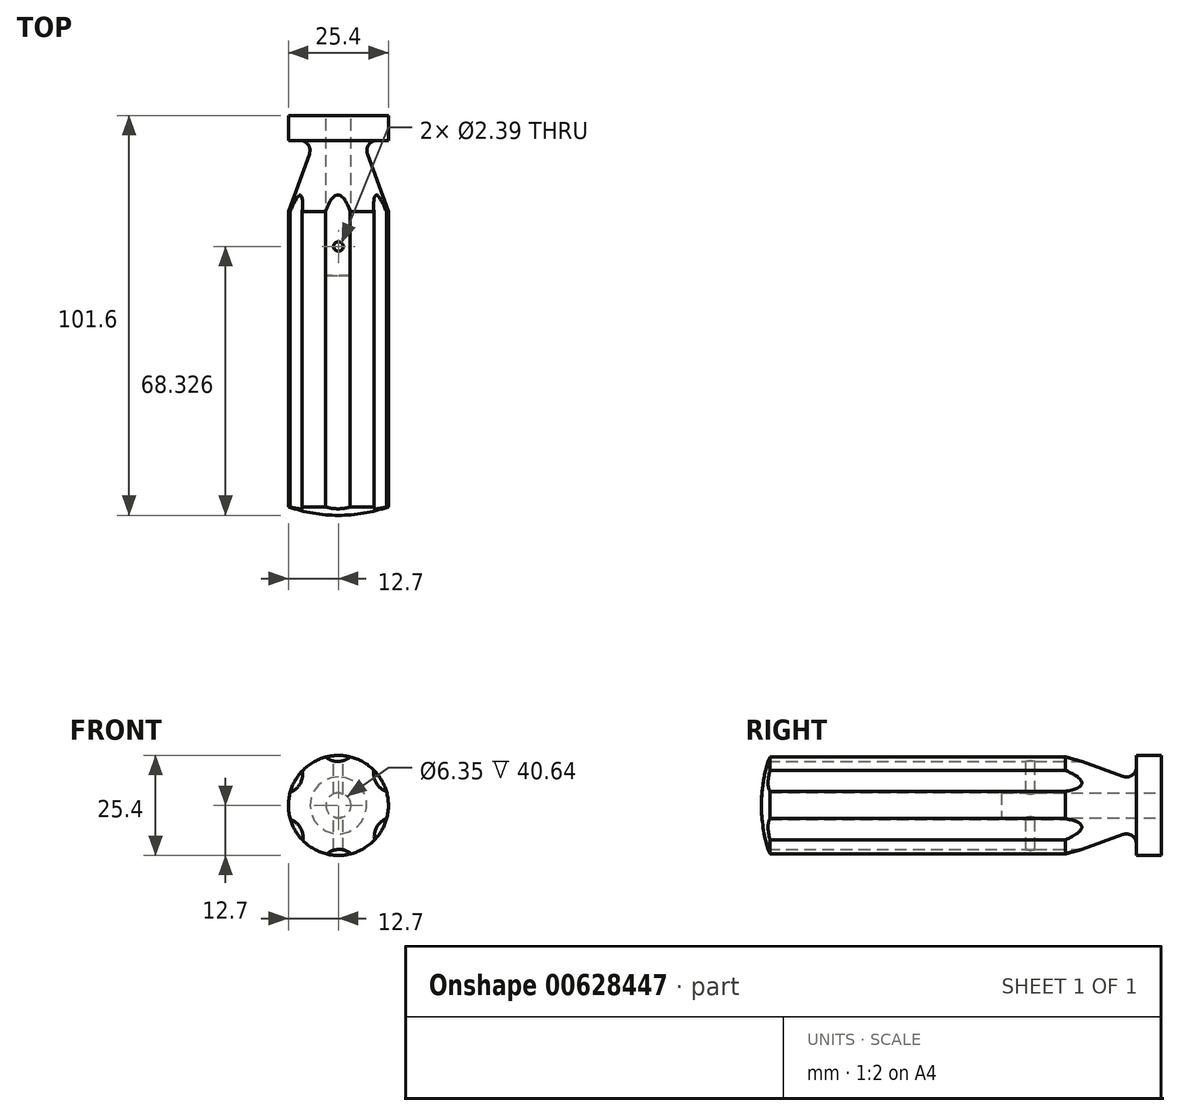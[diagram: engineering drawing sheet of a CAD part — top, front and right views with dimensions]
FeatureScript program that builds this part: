
annotation { "Feature Type Name" : "Feature", "Feature Type Description" : "" }
export const myFeature = defineFeature(function(context is Context, id is Id, definition is map)
    precondition{}
    {
        {
            var Q0;
            Q0=qCreatedBy(makeId("Right.planeOp"),FACE);
            var sketch = newSketch(context, id + "F0", { "sketchPlane" : qUnion([Q0])});
            skLineSegment(sketch, "E0", {"start": v(0, 3.18) * mm, "end": v(-40.64, 3.18) * mm});
            skLineSegment(sketch, "E1", {"start": v(-40.64, 3.18) * mm, "end": v(-40.64, 0) * mm});
            skLineSegment(sketch, "E2", {"start": v(-40.64, 0) * mm, "end": v(-101.6, 0) * mm});
            skLineSegment(sketch, "E3", {"start": v(-99.42, 12.7) * mm, "end": v(-24.38, 12.7) * mm});
            skLineSegment(sketch, "E4", {"start": v(-24.38, 12.7) * mm, "end": v(-9.76, 7.38) * mm});
            skLineSegment(sketch, "E5", {"start": v(-6.35, 9.76) * mm, "end": v(-6.35, 12.7) * mm});
            skLineSegment(sketch, "E6", {"start": v(-6.35, 12.7) * mm, "end": v(0, 12.7) * mm});
            skLineSegment(sketch, "E7", {"start": v(0, 12.7) * mm, "end": v(0, 3.18) * mm});
            skPoint(sketch, "E8.visualSharp", {"position": v(-6.35, 6.14) * mm});
            skArc(sketch, "E8.filletArc", {"start": v(-9.76, 7.38) * mm, "mid": v(-7.43, 7.68) * mm, "end": v(-6.35, 9.76) * mm});
            skArc(sketch, "E9", {"start": v(-99.42, 12.7) * mm, "mid": v(-101.05, 6.44) * mm, "end": v(-101.6, 0) * mm});
            skSolve(sketch);
        }
        {
            var Q0;
            Q0 = qSketchRegion(id + "F0", true);
            var Q1;
            Q1=sQuery(id+"F0.wireOp",EDGE,"E2");
            revolve(context, id + "F1", {"entities" : qUnion([Q0]), "axis" : qUnion([Q1]), "revolveType" : RevolveType.FULL});
        }
        {
            var Q0;
            Q0=qCreatedBy(makeId("Front.planeOp"),FACE);
            var sketch = newSketch(context, id + "F2", { "sketchPlane" : qUnion([Q0])});
            skCircle(sketch, "E10", {"center": v(0, 0) * mm, "radius": 16 * mm, "construction": true});
            skCircle(sketch, "E11", {"center": v(13.94, -7.86) * mm, "radius": 4.83 * mm});
            skCircle(sketch, "E12.1.0", {"center": v(13.78, 8.14) * mm, "radius": 4.83 * mm});
            skCircle(sketch, "E12.2.0", {"center": v(-0.16, 16) * mm, "radius": 4.83 * mm});
            skCircle(sketch, "E12.3.0", {"center": v(-13.94, 7.86) * mm, "radius": 4.83 * mm});
            skCircle(sketch, "E12.4.0", {"center": v(-13.78, -8.14) * mm, "radius": 4.83 * mm});
            skCircle(sketch, "E12.5.0", {"center": v(0.16, -16) * mm, "radius": 4.83 * mm});
            skSolve(sketch);
        }
        {
            var Q0;
            Q0=makeQuery(id+"F2.imprint","IMPRINT",FACE,{"disambiguationData":[TD([[makeQuery(id+"F2.imprint","IMPRINT",EDGE,{"derivedFrom":sQuery(id+"F2.wireOp",EDGE,"E12.2.0")}),1.0]])]});
            var Q1;
            Q1=makeQuery(id+"F2.imprint","IMPRINT",FACE,{"disambiguationData":[TD([[makeQuery(id+"F2.imprint","IMPRINT",EDGE,{"derivedFrom":sQuery(id+"F2.wireOp",EDGE,"E12.1.0")}),1.0]])]});
            var Q2;
            Q2=makeQuery(id+"F2.imprint","IMPRINT",FACE,{"disambiguationData":[TD([[makeQuery(id+"F2.imprint","IMPRINT",EDGE,{"derivedFrom":sQuery(id+"F2.wireOp",EDGE,"E11")}),1.0]])]});
            var Q3;
            Q3=makeQuery(id+"F2.imprint","IMPRINT",FACE,{"disambiguationData":[TD([[makeQuery(id+"F2.imprint","IMPRINT",EDGE,{"derivedFrom":sQuery(id+"F2.wireOp",EDGE,"E12.5.0")}),1.0]])]});
            var Q4;
            Q4=makeQuery(id+"F2.imprint","IMPRINT",FACE,{"disambiguationData":[TD([[makeQuery(id+"F2.imprint","IMPRINT",EDGE,{"derivedFrom":sQuery(id+"F2.wireOp",EDGE,"E12.4.0")}),1.0]])]});
            var Q5;
            Q5=makeQuery(id+"F2.imprint","IMPRINT",FACE,{"disambiguationData":[TD([[makeQuery(id+"F2.imprint","IMPRINT",EDGE,{"derivedFrom":sQuery(id+"F2.wireOp",EDGE,"E12.3.0")}),1.0]])]});
            extrude(context, id + "F3", {"entities" : qUnion([Q0, Q1, Q2, Q3, Q4, Q5]), "operationType" : NewBodyOperationType.REMOVE, "endBound" : BoundingType.THROUGH_ALL, "depth" : 25.4 * mm, "offsetDistance" : 25.4 * mm, "hasSecondDirection" : true, "secondDirectionOppositeDirection" : false, "secondDirectionDepth" : 7.62 * mm});
        }
        {
            var Q0;
            Q0=qCreatedBy(makeId("Top.planeOp"),FACE);
            var sketch = newSketch(context, id + "F4", { "sketchPlane" : qUnion([Q0])});
            skCircle(sketch, "E13", {"center": v(0, -33.27) * mm, "radius": 1.2 * mm});
            skSolve(sketch);
        }
        {
            var Q0;
            Q0 = qSketchRegion(id + "F4", true);
            extrude(context, id + "F5", {"entities" : qUnion([Q0]), "operationType" : NewBodyOperationType.REMOVE, "endBound" : BoundingType.SYMMETRIC, "oppositeDirection" : true, "depth" : 25.4 * mm, "offsetDistance" : 25.4 * mm});
        }
    });
